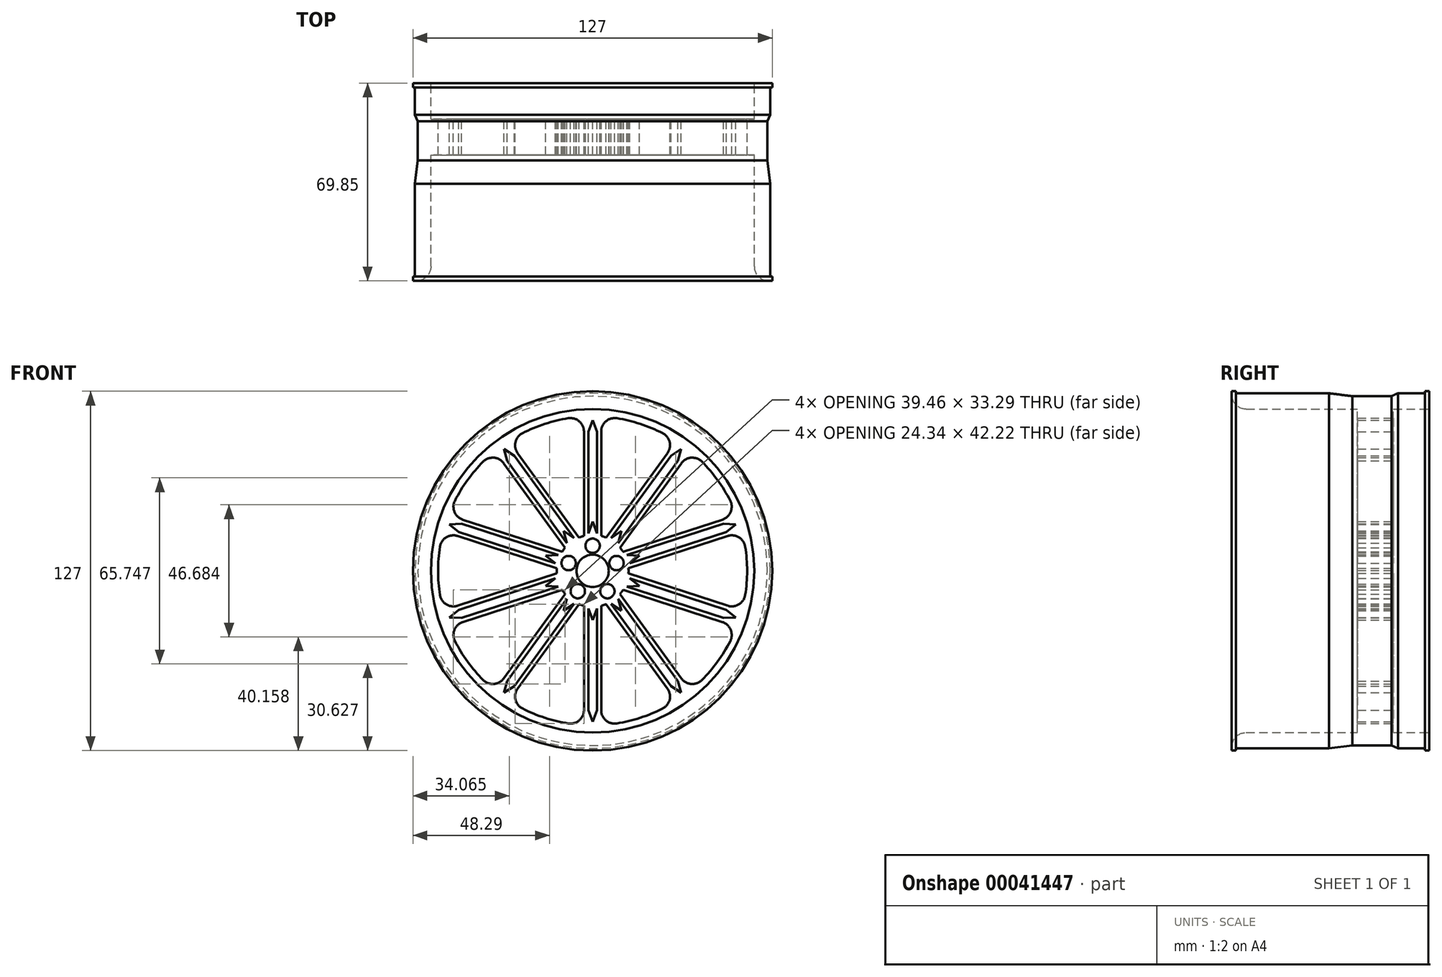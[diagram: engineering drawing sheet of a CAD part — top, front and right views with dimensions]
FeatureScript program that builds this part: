
annotation { "Feature Type Name" : "Feature", "Feature Type Description" : "" }
export const myFeature = defineFeature(function(context is Context, id is Id, definition is map)
    precondition{}
    {
        {
            var Q0;
            Q0=qCreatedBy(makeId("Front.planeOp"),FACE);
            var sketch = newSketch(context, id + "F0", { "sketchPlane" : qUnion([Q0])});
            skCircle(sketch, "E0", {"center": v(0, 0) * mm, "radius": 63.5 * mm});
            skCircle(sketch, "E1", {"center": v(0, 0) * mm, "radius": 57.15 * mm});
            skSolve(sketch);
        }
        {
            var Q0;
            Q0=qCreatedBy(makeId("Front.planeOp"),FACE);
            var sketch = newSketch(context, id + "F1", { "sketchPlane" : qUnion([Q0])});
            skCircle(sketch, "E2", {"center": v(0, 0) * mm, "radius": 57.15 * mm});
            skArc(sketch, "E3", {"start": v(4.8, 11.76) * mm, "mid": v(3.92, 12.08) * mm, "end": v(3.04, 12.33) * mm});
            skLineSegment(sketch, "E4", {"start": v(-3.04, 12.33) * mm, "end": v(-3.04, 49.21) * mm});
            skLineSegment(sketch, "E5.MirrorCS", {"start": v(3.04, 12.33) * mm, "end": v(3.04, 49.21) * mm});
            skArc(sketch, "E6", {"start": v(-38.63, 38.6) * mm, "mid": v(-44.18, 32.1) * mm, "end": v(-48.65, 24.81) * mm});
            skPoint(sketch, "E7.orphan", {"position": v(-3.04, 63.3) * mm});
            skPoint(sketch, "E8.orphan", {"position": v(3.04, 63.3) * mm});
            skPoint(sketch, "E9.orphan", {"position": v(3.04, 0) * mm});
            skPoint(sketch, "E10.orphan", {"position": v(-3.04, 0) * mm});
            skLineSegment(sketch, "E11.1.0", {"start": v(-4.8, 11.76) * mm, "end": v(-26.47, 41.6) * mm});
            skLineSegment(sketch, "E11.1.1", {"start": v(-9.7, 8.2) * mm, "end": v(-31.38, 38.03) * mm});
            skLineSegment(sketch, "E11.2.0", {"start": v(-10.79, 6.7) * mm, "end": v(-45.87, 18.1) * mm});
            skLineSegment(sketch, "E11.2.1", {"start": v(-12.67, 0.92) * mm, "end": v(-47.74, 12.32) * mm});
            skLineSegment(sketch, "E12.1.3.0", {"start": v(-12.67, -0.92) * mm, "end": v(-47.74, -12.32) * mm});
            skLineSegment(sketch, "E12.3.3.0", {"start": v(-10.79, -6.7) * mm, "end": v(-45.87, -18.1) * mm});
            skLineSegment(sketch, "E12.1.4.0", {"start": v(-9.7, -8.2) * mm, "end": v(-31.38, -38.03) * mm});
            skLineSegment(sketch, "E12.3.4.0", {"start": v(-4.8, -11.76) * mm, "end": v(-26.47, -41.6) * mm});
            skLineSegment(sketch, "E12.1.5.0", {"start": v(-3.04, -12.33) * mm, "end": v(-3.04, -49.21) * mm});
            skLineSegment(sketch, "E12.3.5.0", {"start": v(3.04, -12.33) * mm, "end": v(3.04, -49.21) * mm});
            skLineSegment(sketch, "E12.1.6.0", {"start": v(4.8, -11.76) * mm, "end": v(26.47, -41.6) * mm});
            skLineSegment(sketch, "E12.3.6.0", {"start": v(9.7, -8.2) * mm, "end": v(31.38, -38.03) * mm});
            skLineSegment(sketch, "E12.1.7.0", {"start": v(10.79, -6.7) * mm, "end": v(45.87, -18.1) * mm});
            skLineSegment(sketch, "E12.3.7.0", {"start": v(12.67, -0.92) * mm, "end": v(47.74, -12.32) * mm});
            skLineSegment(sketch, "E12.1.8.0", {"start": v(12.67, 0.92) * mm, "end": v(47.74, 12.32) * mm});
            skLineSegment(sketch, "E12.3.8.0", {"start": v(10.79, 6.7) * mm, "end": v(45.87, 18.1) * mm});
            skLineSegment(sketch, "E12.1.9.0", {"start": v(9.7, 8.2) * mm, "end": v(31.38, 38.03) * mm});
            skLineSegment(sketch, "E12.3.9.0", {"start": v(4.8, 11.76) * mm, "end": v(26.47, 41.6) * mm});
            skArc(sketch, "E13.trimOffspring", {"start": v(-53.94, 8.52) * mm, "mid": v(-54.61, 0) * mm, "end": v(-53.94, -8.52) * mm});
            skArc(sketch, "E14.trimOffspring", {"start": v(-8.57, 53.93) * mm, "mid": v(-16.88, 51.94) * mm, "end": v(-24.77, 48.67) * mm});
            skArc(sketch, "E15.trimOffspring", {"start": v(24.77, 48.67) * mm, "mid": v(16.88, 51.94) * mm, "end": v(8.57, 53.93) * mm});
            skArc(sketch, "E16.trimOffspring", {"start": v(-48.65, -24.81) * mm, "mid": v(-44.18, -32.1) * mm, "end": v(-38.63, -38.6) * mm});
            skArc(sketch, "E17.trimOffspring", {"start": v(-24.77, -48.67) * mm, "mid": v(-16.88, -51.94) * mm, "end": v(-8.57, -53.93) * mm});
            skArc(sketch, "E18.trimOffspring", {"start": v(8.57, -53.93) * mm, "mid": v(16.88, -51.94) * mm, "end": v(24.77, -48.67) * mm});
            skArc(sketch, "E19.trimOffspring", {"start": v(38.63, -38.6) * mm, "mid": v(44.18, -32.1) * mm, "end": v(48.65, -24.81) * mm});
            skArc(sketch, "E20.trimOffspring", {"start": v(53.94, -8.52) * mm, "mid": v(54.61, 0) * mm, "end": v(53.94, 8.52) * mm});
            skArc(sketch, "E21.trimOffspring", {"start": v(48.65, 24.81) * mm, "mid": v(44.18, 32.1) * mm, "end": v(38.63, 38.6) * mm});
            skArc(sketch, "E22.trimOffspring", {"start": v(-3.04, 12.33) * mm, "mid": v(-3.92, 12.08) * mm, "end": v(-4.8, 11.76) * mm});
            skArc(sketch, "E23.trimOffspring", {"start": v(-9.7, 8.2) * mm, "mid": v(-10.27, 7.46) * mm, "end": v(-10.79, 6.7) * mm});
            skArc(sketch, "E24.trimOffspring", {"start": v(-12.67, 0.92) * mm, "mid": v(-12.7, 0) * mm, "end": v(-12.67, -0.92) * mm});
            skArc(sketch, "E25.trimOffspring", {"start": v(-10.79, -6.7) * mm, "mid": v(-10.27, -7.46) * mm, "end": v(-9.7, -8.2) * mm});
            skArc(sketch, "E26.trimOffspring", {"start": v(-4.8, -11.76) * mm, "mid": v(-3.92, -12.08) * mm, "end": v(-3.04, -12.33) * mm});
            skArc(sketch, "E27.trimOffspring", {"start": v(3.04, -12.33) * mm, "mid": v(3.92, -12.08) * mm, "end": v(4.8, -11.76) * mm});
            skArc(sketch, "E28.trimOffspring", {"start": v(9.7, -8.2) * mm, "mid": v(10.27, -7.46) * mm, "end": v(10.79, -6.7) * mm});
            skArc(sketch, "E29.trimOffspring", {"start": v(10.79, 6.7) * mm, "mid": v(10.27, 7.46) * mm, "end": v(9.7, 8.2) * mm});
            skArc(sketch, "E30.trimOffspring", {"start": v(12.67, -0.92) * mm, "mid": v(12.7, 0) * mm, "end": v(12.67, 0.92) * mm});
            skPoint(sketch, "E31.visualSharp", {"position": v(-52.8, 13.96) * mm});
            skArc(sketch, "E31.filletArc", {"start": v(-47.74, 12.32) * mm, "mid": v(-51.72, 11.85) * mm, "end": v(-53.94, 8.52) * mm});
            skPoint(sketch, "E32.visualSharp", {"position": v(-52.8, -13.96) * mm});
            skArc(sketch, "E32.filletArc", {"start": v(-53.94, -8.52) * mm, "mid": v(-51.72, -11.85) * mm, "end": v(-47.74, -12.32) * mm});
            skPoint(sketch, "E33.visualSharp", {"position": v(-50.92, -19.74) * mm});
            skArc(sketch, "E33.filletArc", {"start": v(-45.87, -18.1) * mm, "mid": v(-48.8, -20.81) * mm, "end": v(-48.65, -24.81) * mm});
            skPoint(sketch, "E34.visualSharp", {"position": v(-34.5, -42.33) * mm});
            skArc(sketch, "E34.filletArc", {"start": v(-38.63, -38.6) * mm, "mid": v(-34.88, -39.99) * mm, "end": v(-31.38, -38.03) * mm});
            skPoint(sketch, "E35.visualSharp", {"position": v(-29.6, -45.9) * mm});
            skArc(sketch, "E35.filletArc", {"start": v(-26.47, -41.6) * mm, "mid": v(-27.25, -45.53) * mm, "end": v(-24.77, -48.67) * mm});
            skPoint(sketch, "E36.visualSharp", {"position": v(-3.04, -54.53) * mm});
            skArc(sketch, "E36.filletArc", {"start": v(-8.57, -53.93) * mm, "mid": v(-4.71, -52.85) * mm, "end": v(-3.04, -49.21) * mm});
            skPoint(sketch, "E37.visualSharp", {"position": v(3.04, -54.53) * mm});
            skArc(sketch, "E37.filletArc", {"start": v(3.04, -49.21) * mm, "mid": v(4.71, -52.85) * mm, "end": v(8.57, -53.93) * mm});
            skPoint(sketch, "E38.visualSharp", {"position": v(29.6, -45.9) * mm});
            skArc(sketch, "E38.filletArc", {"start": v(24.77, -48.67) * mm, "mid": v(27.25, -45.53) * mm, "end": v(26.47, -41.6) * mm});
            skPoint(sketch, "E39.visualSharp", {"position": v(34.5, -42.33) * mm});
            skArc(sketch, "E39.filletArc", {"start": v(31.38, -38.03) * mm, "mid": v(34.88, -39.99) * mm, "end": v(38.63, -38.6) * mm});
            skPoint(sketch, "E40.visualSharp", {"position": v(50.92, -19.74) * mm});
            skArc(sketch, "E40.filletArc", {"start": v(48.65, -24.81) * mm, "mid": v(48.8, -20.81) * mm, "end": v(45.87, -18.1) * mm});
            skPoint(sketch, "E41.visualSharp", {"position": v(52.8, -13.96) * mm});
            skArc(sketch, "E41.filletArc", {"start": v(47.74, -12.32) * mm, "mid": v(51.72, -11.85) * mm, "end": v(53.94, -8.52) * mm});
            skPoint(sketch, "E42.visualSharp", {"position": v(52.8, 13.96) * mm});
            skArc(sketch, "E42.filletArc", {"start": v(53.94, 8.52) * mm, "mid": v(51.72, 11.85) * mm, "end": v(47.74, 12.32) * mm});
            skPoint(sketch, "E43.visualSharp", {"position": v(50.92, 19.74) * mm});
            skArc(sketch, "E43.filletArc", {"start": v(45.87, 18.1) * mm, "mid": v(48.8, 20.81) * mm, "end": v(48.65, 24.81) * mm});
            skPoint(sketch, "E44.visualSharp", {"position": v(-50.92, 19.74) * mm});
            skArc(sketch, "E44.filletArc", {"start": v(-48.65, 24.81) * mm, "mid": v(-48.8, 20.81) * mm, "end": v(-45.87, 18.1) * mm});
            skPoint(sketch, "E45.visualSharp", {"position": v(-34.5, 42.33) * mm});
            skArc(sketch, "E45.filletArc", {"start": v(-31.38, 38.03) * mm, "mid": v(-34.88, 39.99) * mm, "end": v(-38.63, 38.6) * mm});
            skPoint(sketch, "E46.visualSharp", {"position": v(-29.6, 45.9) * mm});
            skArc(sketch, "E46.filletArc", {"start": v(-24.77, 48.67) * mm, "mid": v(-27.25, 45.53) * mm, "end": v(-26.47, 41.6) * mm});
            skPoint(sketch, "E47.visualSharp", {"position": v(-3.04, 54.53) * mm});
            skArc(sketch, "E47.filletArc", {"start": v(-3.04, 49.21) * mm, "mid": v(-4.71, 52.85) * mm, "end": v(-8.57, 53.93) * mm});
            skPoint(sketch, "E48.visualSharp", {"position": v(3.04, 54.53) * mm});
            skArc(sketch, "E48.filletArc", {"start": v(8.57, 53.93) * mm, "mid": v(4.71, 52.85) * mm, "end": v(3.04, 49.21) * mm});
            skPoint(sketch, "E49.visualSharp", {"position": v(29.6, 45.9) * mm});
            skArc(sketch, "E49.filletArc", {"start": v(26.47, 41.6) * mm, "mid": v(27.25, 45.53) * mm, "end": v(24.77, 48.67) * mm});
            skPoint(sketch, "E50.visualSharp", {"position": v(34.5, 42.33) * mm});
            skArc(sketch, "E50.filletArc", {"start": v(38.63, 38.6) * mm, "mid": v(34.88, 39.99) * mm, "end": v(31.38, 38.03) * mm});
            skCircle(sketch, "E51", {"center": v(0, 8.9) * mm, "radius": 2.54 * mm});
            skCircle(sketch, "E52.1.0", {"center": v(-8.45, 2.75) * mm, "radius": 2.54 * mm});
            skCircle(sketch, "E52.2.0", {"center": v(-5.23, -7.2) * mm, "radius": 2.54 * mm});
            skCircle(sketch, "E52.3.0", {"center": v(5.23, -7.2) * mm, "radius": 2.54 * mm});
            skCircle(sketch, "E52.4.0", {"center": v(8.45, 2.75) * mm, "radius": 2.54 * mm});
            skCircle(sketch, "E53", {"center": v(0, 0) * mm, "radius": 5.72 * mm});
            skLineSegment(sketch, "E54", {"start": v(1.52, 49.21) * mm, "end": v(1.52, 13.28) * mm});
            skLineSegment(sketch, "E55", {"start": v(1.52, 13.28) * mm, "end": v(0, 17.37) * mm});
            skLineSegment(sketch, "E56", {"start": v(1.52, 49.21) * mm, "end": v(0, 53.26) * mm});
            skLineSegment(sketch, "E57.MirrorCS", {"start": v(-1.52, 49.21) * mm, "end": v(-1.52, 13.28) * mm});
            skLineSegment(sketch, "E58.MirrorCS", {"start": v(-1.52, 49.21) * mm, "end": v(0, 53.26) * mm});
            skLineSegment(sketch, "E59.MirrorCS", {"start": v(-1.52, 13.28) * mm, "end": v(0, 17.37) * mm});
            skPoint(sketch, "E60.end.orphan", {"position": v(0, 49.21) * mm});
            skLineSegment(sketch, "E61.1.0", {"start": v(-30.16, 38.92) * mm, "end": v(-31.3, 43.1) * mm});
            skLineSegment(sketch, "E61.1.1", {"start": v(-27.7, 40.7) * mm, "end": v(-31.3, 43.1) * mm});
            skLineSegment(sketch, "E61.1.2", {"start": v(-27.7, 40.7) * mm, "end": v(-6.58, 11.64) * mm});
            skLineSegment(sketch, "E61.1.3", {"start": v(-6.58, 11.64) * mm, "end": v(-10.21, 14.06) * mm});
            skLineSegment(sketch, "E61.1.4", {"start": v(-9.04, 9.85) * mm, "end": v(-10.21, 14.06) * mm});
            skLineSegment(sketch, "E61.1.5", {"start": v(-30.16, 38.92) * mm, "end": v(-9.04, 9.85) * mm});
            skLineSegment(sketch, "E61.2.0", {"start": v(-47.27, 13.76) * mm, "end": v(-50.66, 16.46) * mm});
            skLineSegment(sketch, "E61.2.1", {"start": v(-46.34, 16.65) * mm, "end": v(-50.66, 16.46) * mm});
            skLineSegment(sketch, "E61.2.2", {"start": v(-46.34, 16.65) * mm, "end": v(-12.16, 5.55) * mm});
            skLineSegment(sketch, "E61.2.3", {"start": v(-12.16, 5.55) * mm, "end": v(-16.52, 5.37) * mm});
            skLineSegment(sketch, "E61.2.4", {"start": v(-13.1, 2.66) * mm, "end": v(-16.52, 5.37) * mm});
            skLineSegment(sketch, "E61.2.5", {"start": v(-47.27, 13.76) * mm, "end": v(-13.1, 2.66) * mm});
            skLineSegment(sketch, "E62.1.3.0", {"start": v(-46.34, -16.65) * mm, "end": v(-50.66, -16.46) * mm});
            skLineSegment(sketch, "E62.3.3.0", {"start": v(-47.27, -13.76) * mm, "end": v(-50.66, -16.46) * mm});
            skLineSegment(sketch, "E62.6.3.0", {"start": v(-47.27, -13.76) * mm, "end": v(-13.1, -2.66) * mm});
            skLineSegment(sketch, "E62.9.3.0", {"start": v(-13.1, -2.66) * mm, "end": v(-16.52, -5.37) * mm});
            skLineSegment(sketch, "E62.12.3.0", {"start": v(-12.16, -5.55) * mm, "end": v(-16.52, -5.37) * mm});
            skLineSegment(sketch, "E62.15.3.0", {"start": v(-46.34, -16.65) * mm, "end": v(-12.16, -5.55) * mm});
            skLineSegment(sketch, "E62.1.4.0", {"start": v(-27.7, -40.7) * mm, "end": v(-31.3, -43.1) * mm});
            skLineSegment(sketch, "E62.3.4.0", {"start": v(-30.16, -38.92) * mm, "end": v(-31.3, -43.1) * mm});
            skLineSegment(sketch, "E62.6.4.0", {"start": v(-30.16, -38.92) * mm, "end": v(-9.04, -9.85) * mm});
            skLineSegment(sketch, "E62.9.4.0", {"start": v(-9.04, -9.85) * mm, "end": v(-10.21, -14.06) * mm});
            skLineSegment(sketch, "E62.12.4.0", {"start": v(-6.58, -11.64) * mm, "end": v(-10.21, -14.06) * mm});
            skLineSegment(sketch, "E62.15.4.0", {"start": v(-27.7, -40.7) * mm, "end": v(-6.58, -11.64) * mm});
            skLineSegment(sketch, "E62.1.5.0", {"start": v(1.52, -49.21) * mm, "end": v(0, -53.26) * mm});
            skLineSegment(sketch, "E62.3.5.0", {"start": v(-1.52, -49.21) * mm, "end": v(0, -53.26) * mm});
            skLineSegment(sketch, "E62.6.5.0", {"start": v(-1.52, -49.21) * mm, "end": v(-1.52, -13.28) * mm});
            skLineSegment(sketch, "E62.9.5.0", {"start": v(-1.52, -13.28) * mm, "end": v(0, -17.37) * mm});
            skLineSegment(sketch, "E62.12.5.0", {"start": v(1.52, -13.28) * mm, "end": v(0, -17.37) * mm});
            skLineSegment(sketch, "E62.15.5.0", {"start": v(1.52, -49.21) * mm, "end": v(1.52, -13.28) * mm});
            skLineSegment(sketch, "E62.1.6.0", {"start": v(30.16, -38.92) * mm, "end": v(31.3, -43.1) * mm});
            skLineSegment(sketch, "E62.3.6.0", {"start": v(27.7, -40.7) * mm, "end": v(31.3, -43.1) * mm});
            skLineSegment(sketch, "E62.6.6.0", {"start": v(27.7, -40.7) * mm, "end": v(6.58, -11.64) * mm});
            skLineSegment(sketch, "E62.9.6.0", {"start": v(6.58, -11.64) * mm, "end": v(10.21, -14.06) * mm});
            skLineSegment(sketch, "E62.12.6.0", {"start": v(9.04, -9.85) * mm, "end": v(10.21, -14.06) * mm});
            skLineSegment(sketch, "E62.15.6.0", {"start": v(30.16, -38.92) * mm, "end": v(9.04, -9.85) * mm});
            skLineSegment(sketch, "E62.1.7.0", {"start": v(47.27, -13.76) * mm, "end": v(50.66, -16.46) * mm});
            skLineSegment(sketch, "E62.3.7.0", {"start": v(46.34, -16.65) * mm, "end": v(50.66, -16.46) * mm});
            skLineSegment(sketch, "E62.6.7.0", {"start": v(46.34, -16.65) * mm, "end": v(12.16, -5.55) * mm});
            skLineSegment(sketch, "E62.9.7.0", {"start": v(12.16, -5.55) * mm, "end": v(16.52, -5.37) * mm});
            skLineSegment(sketch, "E62.12.7.0", {"start": v(13.1, -2.66) * mm, "end": v(16.52, -5.37) * mm});
            skLineSegment(sketch, "E62.15.7.0", {"start": v(47.27, -13.76) * mm, "end": v(13.1, -2.66) * mm});
            skLineSegment(sketch, "E62.1.8.0", {"start": v(46.34, 16.65) * mm, "end": v(50.66, 16.46) * mm});
            skLineSegment(sketch, "E62.3.8.0", {"start": v(47.27, 13.76) * mm, "end": v(50.66, 16.46) * mm});
            skLineSegment(sketch, "E62.6.8.0", {"start": v(47.27, 13.76) * mm, "end": v(13.1, 2.66) * mm});
            skLineSegment(sketch, "E62.9.8.0", {"start": v(13.1, 2.66) * mm, "end": v(16.52, 5.37) * mm});
            skLineSegment(sketch, "E62.12.8.0", {"start": v(12.16, 5.55) * mm, "end": v(16.52, 5.37) * mm});
            skLineSegment(sketch, "E62.15.8.0", {"start": v(46.34, 16.65) * mm, "end": v(12.16, 5.55) * mm});
            skLineSegment(sketch, "E62.1.9.0", {"start": v(27.7, 40.7) * mm, "end": v(31.3, 43.1) * mm});
            skLineSegment(sketch, "E62.3.9.0", {"start": v(30.16, 38.92) * mm, "end": v(31.3, 43.1) * mm});
            skLineSegment(sketch, "E62.6.9.0", {"start": v(30.16, 38.92) * mm, "end": v(9.04, 9.85) * mm});
            skLineSegment(sketch, "E62.9.9.0", {"start": v(9.04, 9.85) * mm, "end": v(10.21, 14.06) * mm});
            skLineSegment(sketch, "E62.12.9.0", {"start": v(6.58, 11.64) * mm, "end": v(10.21, 14.06) * mm});
            skLineSegment(sketch, "E62.15.9.0", {"start": v(27.7, 40.7) * mm, "end": v(6.58, 11.64) * mm});
            skSolve(sketch);
        }
        {
            var Q0;
            Q0=makeQuery(id+"F1.imprint","IMPRINT",FACE,{"disambiguationData":[TD([[makeQuery(id+"F1.imprint","IMPRINT",EDGE,{"derivedFrom":sQuery(id+"F1.wireOp",EDGE,"E2")}),1.0]])]});
            extrude(context, id + "F2", {"entities" : qUnion([Q0]), "endBound" : BoundingType.SYMMETRIC, "depth" : 12.7 * mm});
        }
        {
            var Q0;
            Q0=makeQuery(id+"F0.imprint","IMPRINT",FACE,{"disambiguationData":[TD([[makeQuery(id+"F0.imprint","IMPRINT",EDGE,{"derivedFrom":sQuery(id+"F0.wireOp",EDGE,"E0")}),1.0]])]});
            extrude(context, id + "F3", {"entities" : qUnion([Q0]), "operationType" : NewBodyOperationType.ADD, "depth" : 50.8 * mm, "hasSecondDirection" : true, "secondDirectionOppositeDirection" : true, "secondDirectionDepth" : 19.05 * mm});
        }
        {
            var Q0;
            Q0=qCreatedBy(makeId("Right.planeOp"),FACE);
            var sketch = newSketch(context, id + "F4", { "sketchPlane" : qUnion([Q0])});
            skLineSegment(sketch, "E63", {"start": v(0, 61.74) * mm, "end": v(5.63, 61.74) * mm});
            skLineSegment(sketch, "E64", {"start": v(5.63, 61.74) * mm, "end": v(7.9, 62.75) * mm});
            skLineSegment(sketch, "E65", {"start": v(7.9, 62.75) * mm, "end": v(17.53, 62.75) * mm});
            skLineSegment(sketch, "E66", {"start": v(17.53, 62.75) * mm, "end": v(17.53, 63.5) * mm});
            skLineSegment(sketch, "E67", {"start": v(17.53, 63.5) * mm, "end": v(-49.28, 63.5) * mm});
            skLineSegment(sketch, "E68", {"start": v(-49.28, 63.5) * mm, "end": v(-49.28, 62.75) * mm});
            skLineSegment(sketch, "E69", {"start": v(-49.28, 62.75) * mm, "end": v(-16.46, 62.75) * mm});
            skLineSegment(sketch, "E70", {"start": v(-16.46, 62.75) * mm, "end": v(-8.2, 61.74) * mm});
            skLineSegment(sketch, "E71", {"start": v(-8.2, 61.74) * mm, "end": v(0, 61.74) * mm});
            skPoint(sketch, "E72.orphan", {"position": v(0, 63.56) * mm});
            skLineSegment(sketch, "E73", {"start": v(-64.51, 0) * mm, "end": v(40.85, 0) * mm});
            skSolve(sketch);
        }
        {
            var Q0;
            Q0 = qSketchRegion(id + "F4", true);
            var Q1;
            Q1=sQuery(id+"F4.wireOp",EDGE,"E73");
            revolve(context, id + "F5", {"operationType" : NewBodyOperationType.REMOVE, "entities" : qUnion([Q0]), "axis" : qUnion([Q1]), "revolveType" : RevolveType.FULL, "oppositeDirection" : true});
        }
        {
            var Q0;
            Q0=makeQuery(id+"F3.opExtrude","CAP_EDGE",EDGE,{"disambiguationData":[OSD([sQuery(id+"F0.wireOp",EDGE,"E1")])],"isStart":false});
            fillet(context, id + "F6", {"entities" : qUnion([Q0]), "radius" : 5.08 * mm, "tangentPropagation" : true, "allowEdgeOverflow" : false});
        }
    });
